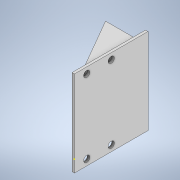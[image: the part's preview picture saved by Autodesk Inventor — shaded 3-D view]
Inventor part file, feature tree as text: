
AUTODESK INVENTOR PART (.ipt)
format: ipt  version: 2021.4 (Build 254397000, 397)  size: 150,528 bytes
history: native  units: mm
features: sketch x7, extrude x3, hole x3
ambient origin geometry x8: Origin, YZ Plane, XZ Plane, XY Plane, X Axis, Y Axis, Z Axis, Center Point
bodies: Body1 (feature_tree)
feature tree (13):
  extrude  "押し出し2"  Depth=60.0mm
  extrude  "押し出し3"  TaperAngle=60.0deg  [1 undecoded]
  hole  "穴2"  [1 undecoded]
  sketch  "スケッチ6"
  hole  "穴4"  [1 undecoded]
  extrude  "押し出し5"  Depth=10.0mm TaperAngle=0.0deg
  hole  "穴5"  [1 undecoded]
  sketch  "スケッチ3"
  sketch  "スケッチ4"
  sketch  "スケッチ5"
  sketch  "スケッチ12"
  sketch  "スケッチ13"
  sketch  "スケッチ14"
note: 4 required parameter values undecoded (feature->parameter linkage not recoverable at this tier; creation-order binding heuristic only, values carry confidence <= 0.55)
